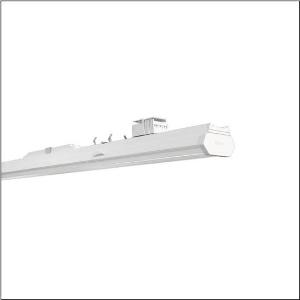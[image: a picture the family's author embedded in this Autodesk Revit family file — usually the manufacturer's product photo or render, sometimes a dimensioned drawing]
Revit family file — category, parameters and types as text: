
# Revit family: licross_11_protected_extreme_mo_51td1bdn68xge
name_source: partatom
category: Lighting Fixtures
units: mm (PartAtom-declared; Revit-internal decimal feet)

## family parameters
Cut with Voids When Loaded = No
Host = Face
Light Source = No
Part Type = Normal
Room Calculation Point = No
Round Connector Dimension = Use Diameter
Shared = No

## types (1)
- --- (1 x LED, 8310 lm, 51.4 W, 6500K)
    Apparent Load = 51 VA
    CIE Flux Codes = 54 82 95 97 100
    Color Rendering = 80
    Color Temperature = 6500K
    Default Elevation = 1800 mm
    Description = Licross 11 Protected extreme MO, luminaire insert, of sheet steel, galvanised, coil coated, white, length: 1.500mm, width: 90mm, height: 101mm, LED rated luminous flux: 8.310lm, light colour: 865, SDCM (Standard Deviation of Colour Matching)MacAdam ≤ 2 SDCM (initial), control gear: DALI 2, with plug, 5-pole, with phase selection, mains connection: 220..240V, AC, 50/60Hz, rated input power: 51W, internal wiring halogen-free, primary optical cover: cover, of PMMA, light emission: direct distribution, primary light characteristic: symmetric, protection rating (complete): IP54, insulation class (complete): insulation class I (protective earthing), certification: CE, ENEC, VDE, UKCA, protection symbol: D if used in an environment with non-conductive dust loads with corresponding accessories, impact resistance: IK06, permissible ambient temperature for indoor applications: -40..+45°C, corresponds to IFS (International Featured Standards) requirements for safety and quality in the food industry, reducing of maximum allowable ambient temperature of 5°C with ceiling mounting, LABS conformity tested according to VDMA 24364:2018-05, The light source and the operating device comply with the requirements of the Ecodesign Regulation (EU) 2019/2020 and are replaceable in accordance with this regulation, packaging unit: 1 piece
    Height = 92 mm
    Lamp = 1 x LED
    Lamp Light Flux = 8310 lm
    Lamp Power = 51.4 W
    Lamp count = 1
    Length = 1500 mm
    Luminous efficacy = 162 lm/W
    Manufacturer = Siteco
    ModVariant = No
    Model = 51TD1BDN68XGE
    Mounting Place = Ceiling
    Mounting Type = Pendant
    Number of Poles = 1
    OnlyDefault = Yes
    Power Factor = 1
    Product Name = Licross 11 Protected extreme MO
    Product group = luminaire insert | ceiling pendant
    ProductGroupID = 901
    Protection Class = Protection class I
    Protection Degree = IP 54
    RLX_Detail_Level = 1
    RLX_Emergency_Light_Flux = 0 lm
    RLX_Emergency_Type = 0
    RLX_Emergency_Type_DB = No
    RlxData = <blob elided: 24617 chars, md5=236c9209>
    Socket = socket
    Standby Power = 0 W
    System Light Flux = 8310 lm
    System Power = 51 W
    Type Comments = factory setting: luminous flux: 100 % | dim-lin: 254 | 341 mA
    Type Image = l_1256145.jpg
    URL = http://relux.com
    VarID = @adj_021477
    Voltage = 0 V
    Weight = 0.00 kg
    Width = 88 mm

## geometry (parser evidence)
native form markers: Blend x4, Sweep x10
no freeform markers — native parametric forms only
